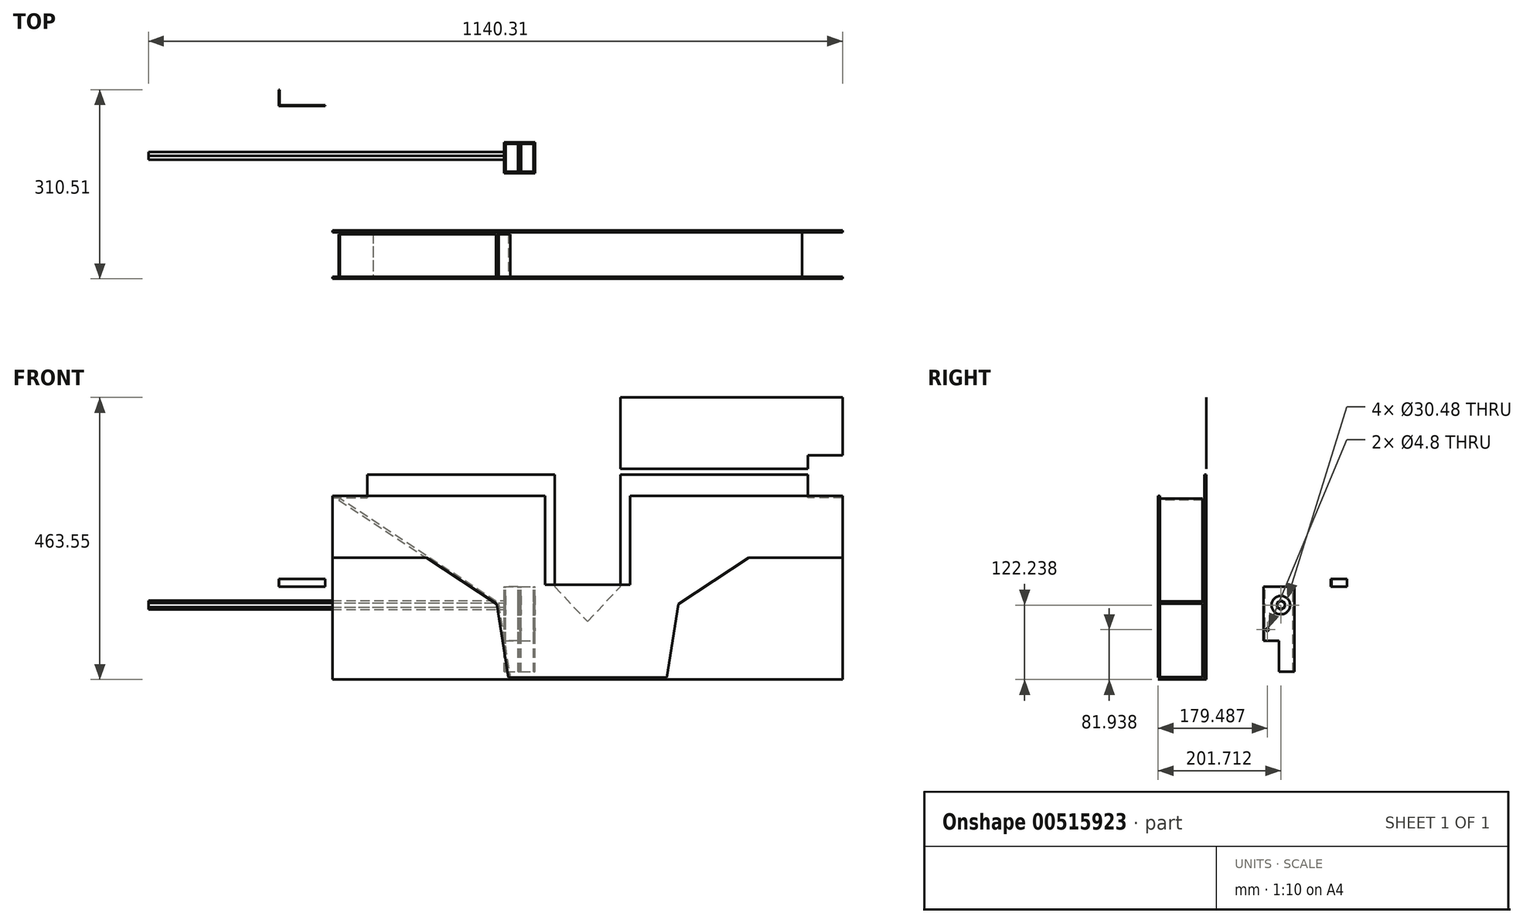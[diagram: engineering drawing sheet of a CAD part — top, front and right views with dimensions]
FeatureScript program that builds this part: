
annotation { "Feature Type Name" : "Feature", "Feature Type Description" : "" }
export const myFeature = defineFeature(function(context is Context, id is Id, definition is map)
    precondition{}
    {
        {
            var Q0;
            Q0=qCreatedBy(makeId("Front.planeOp"),FACE);
            var sketch = newSketch(context, id + "F0", { "sketchPlane" : qUnion([Q0])});
            skLineSegment(sketch, "E0", {"start": v(-365.13, 311.15) * mm, "end": v(-365.13, -152.4) * mm});
            skLineSegment(sketch, "E1", {"start": v(-365.13, -152.4) * mm, "end": v(473.07, -152.4) * mm});
            skLineSegment(sketch, "E2", {"start": v(473.07, 311.15) * mm, "end": v(473.07, -152.4) * mm});
            skLineSegment(sketch, "E3", {"start": v(0, 311.15) * mm, "end": v(0, 0) * mm});
            skLineSegment(sketch, "E4", {"start": v(0, 0) * mm, "end": v(107.95, 0) * mm});
            skLineSegment(sketch, "E5", {"start": v(107.95, 0) * mm, "end": v(107.95, 311.15) * mm});
            skLineSegment(sketch, "E6", {"start": v(0, 311.15) * mm, "end": v(-365.13, 311.15) * mm});
            skLineSegment(sketch, "E7", {"start": v(107.95, 311.15) * mm, "end": v(473.07, 311.15) * mm});
            skLineSegment(sketch, "E8", {"start": v(-365.13, 184.15) * mm, "end": v(0, 184.15) * mm});
            skLineSegment(sketch, "E9", {"start": v(107.95, 184.15) * mm, "end": v(473.07, 184.15) * mm});
            skLineSegment(sketch, "E10", {"start": v(107.95, 193.67) * mm, "end": v(473.07, 193.67) * mm});
            skLineSegment(sketch, "E11", {"start": v(0, 0) * mm, "end": v(53.97, -57.15) * mm});
            skLineSegment(sketch, "E12", {"start": v(53.97, -57.15) * mm, "end": v(107.95, 0) * mm});
            skSolve(sketch);
        }
        {
            var Q0;
            {var subQ1=sQuery(id+"F0.wireOp",EDGE,"E1");Q0=makeQuery(id+"F0.imprint","IMPRINT",FACE,{"disambiguationData":[TD([[makeQuery(id+"F0.imprint","IMPRINT",EDGE,{"derivedFrom":subQ1}),1.0]])]});}
            extrude(context, id + "F1", {"entities" : qUnion([Q0]), "depth" : 3.17 * mm});
        }
        {
            var Q0;
            Q0=makeQuery(id+"F1.opExtrude","SWEPT_FACE",FACE,{"disambiguationData":[OSD([sQuery(id+"F0.wireOp",EDGE,"E1")])]});
            var sketch = newSketch(context, id + "F2", { "sketchPlane" : qUnion([Q0])});
            skLineSegment(sketch, "E13.bottom", {"start": v(-298.45, 3.18) * mm, "end": v(406.4, 3.18) * mm});
            skLineSegment(sketch, "E13.top", {"start": v(-298.45, 79.37) * mm, "end": v(406.4, 79.37) * mm});
            skLineSegment(sketch, "E13.left", {"start": v(406.4, 3.18) * mm, "end": v(406.4, 79.37) * mm});
            skLineSegment(sketch, "E13.right", {"start": v(-298.45, 3.18) * mm, "end": v(-298.45, 79.37) * mm});
            skLineSegment(sketch, "E14", {"start": v(406.4, 3.18) * mm, "end": v(-365.13, 3.18) * mm, "construction": true});
            skLineSegment(sketch, "E15", {"start": v(-298.45, 3.17) * mm, "end": v(473.08, 0) * mm, "construction": true});
            skSolve(sketch);
        }
        {
            var Q0;
            Q0=makeQuery(id+"F2.imprint","IMPRINT",FACE,{"disambiguationData":[TD([[makeQuery(id+"F2.imprint","IMPRINT",EDGE,{"derivedFrom":sQuery(id+"F2.wireOp",EDGE,"E13.bottom")}),1.0]])]});
            extrude(context, id + "F3", {"entities" : qUnion([Q0]), "oppositeDirection" : true, "depth" : 1 / 203.2 * mm});
        }
        {
            var Q0;
            {var subQ0=sQuery(id+"F0.wireOp",EDGE,"E7");Q0=makeQuery(id+"F0.imprint","IMPRINT",FACE,{"disambiguationData":[TD([[makeQuery(id+"F0.imprint","IMPRINT",EDGE,{"derivedFrom":subQ0}),-1.0]])]});}
            extrude(context, id + "F4", {"entities" : qUnion([Q0]), "depth" : 1 / 203.2 * mm});
        }
        {
            var Q0;
            Q0=makeQuery(id+"F3.opExtrude","SWEPT_FACE",FACE,{"disambiguationData":[OSD([sQuery(id+"F2.wireOp",EDGE,"E13.top")])]});
            var sketch = newSketch(context, id + "F5", { "sketchPlane" : qUnion([Q0])});
            skLineSegment(sketch, "E16", {"start": v(-15.88, 149.22) * mm, "end": v(-365.13, 149.22) * mm});
            skLineSegment(sketch, "E17", {"start": v(-365.13, 149.23) * mm, "end": v(-95.25, -28.58) * mm});
            skLineSegment(sketch, "E18", {"start": v(-95.25, -28.57) * mm, "end": v(-76.2, -149.22) * mm});
            skLineSegment(sketch, "E19.MirrorCS", {"start": v(203.2, -28.58) * mm, "end": v(184.15, -149.22) * mm});
            skLineSegment(sketch, "E20.MirrorCS", {"start": v(473.07, 149.23) * mm, "end": v(203.2, -28.58) * mm});
            skLineSegment(sketch, "E21.MirrorCS", {"start": v(123.82, 149.23) * mm, "end": v(473.07, 149.23) * mm});
            skLineSegment(sketch, "E22", {"start": v(-76.2, -149.23) * mm, "end": v(184.15, -149.22) * mm});
            skPoint(sketch, "E23", {"position": v(53.98, -152.4) * mm});
            skLineSegment(sketch, "E24", {"start": v(-15.88, 149.22) * mm, "end": v(-15.88, 3.17) * mm});
            skLineSegment(sketch, "E25", {"start": v(123.82, 149.23) * mm, "end": v(123.82, 3.18) * mm});
            skLineSegment(sketch, "E26", {"start": v(-365.13, 149.22) * mm, "end": v(-365.13, 47.62) * mm});
            skLineSegment(sketch, "E27", {"start": v(-365.13, 47.62) * mm, "end": v(-210.91, 47.62) * mm});
            skLineSegment(sketch, "E28", {"start": v(473.07, 149.23) * mm, "end": v(473.07, 47.62) * mm});
            skLineSegment(sketch, "E29", {"start": v(473.07, 47.62) * mm, "end": v(318.86, 47.62) * mm});
            skLineSegment(sketch, "E30", {"start": v(-95.25, -28.58) * mm, "end": v(203.2, -28.58) * mm, "construction": true});
            skLineSegment(sketch, "E31", {"start": v(123.82, 3.18) * mm, "end": v(-15.88, 3.17) * mm});
            skSolve(sketch);
        }
        {
            var Q0;
            Q0=makeQuery(id+"F5.imprint","IMPRINT",FACE,{"disambiguationData":[TD([[makeQuery(id+"F5.imprint","IMPRINT",EDGE,{"derivedFrom":sQuery(id+"F5.wireOp",EDGE,"E16")}),1.0]])]});
            var Q1;
            {var subQ0=sQuery(id+"F5.wireOp",EDGE,"E26");Q1=makeQuery(id+"F5.imprint","IMPRINT",FACE,{"disambiguationData":[TD([[makeQuery(id+"F5.imprint","IMPRINT",EDGE,{"derivedFrom":subQ0}),1.0]])]});}
            var Q2;
            {var subQ0=sQuery(id+"F5.wireOp",EDGE,"E28");Q2=makeQuery(id+"F5.imprint","IMPRINT",FACE,{"disambiguationData":[TD([[makeQuery(id+"F5.imprint","IMPRINT",EDGE,{"derivedFrom":subQ0}),-1.0]])]});}
            extrude(context, id + "F6", {"entities" : qUnion([Q0, Q1, Q2]), "oppositeDirection" : true, "depth" : 3.17 * mm});
        }
        {
            var Q0;
            Q0=makeQuery(id+"F6.opExtrude","CAP_FACE",FACE,{"disambiguationData":[OSD([sQuery(id+"F5.wireOp",EDGE,"E16"),sQuery(id+"F5.wireOp",EDGE,"E17"),sQuery(id+"F5.wireOp",EDGE,"E18"),sQuery(id+"F5.wireOp",EDGE,"E19.MirrorCS"),sQuery(id+"F5.wireOp",EDGE,"E20.MirrorCS"),sQuery(id+"F5.wireOp",EDGE,"E21.MirrorCS"),sQuery(id+"F5.wireOp",EDGE,"E22"),sQuery(id+"F5.wireOp",EDGE,"E24"),sQuery(id+"F5.wireOp",EDGE,"E25"),sQuery(id+"F5.wireOp",EDGE,"bJVduE53-CYSX-zZap-hoKB-BpQSyu4JU1O0"),sQuery(id+"F5.wireOp",EDGE,"kxEBCK4Z-cyDY-w3D9-cJRx-P5z5Afn2VGam")])],"isStart":false});
            var sketch = newSketch(context, id + "F7", { "sketchPlane" : qUnion([Q0])});
            skLineSegment(sketch, "E32.bottom", {"start": v(95.25, -28.58) * mm, "end": v(92.11, -28.08) * mm});
            skLineSegment(sketch, "E32.top", {"start": v(76.2, -149.23) * mm, "end": v(73.06, -148.73) * mm});
            skLineSegment(sketch, "E32.left", {"start": v(95.25, -28.57) * mm, "end": v(76.2, -149.23) * mm});
            skLineSegment(sketch, "E32.right", {"start": v(92.11, -28.08) * mm, "end": v(73.06, -148.73) * mm});
            skSolve(sketch);
        }
        {
            var Q0;
            Q0 = qSketchRegion(id + "F7", true);
            extrude(context, id + "F8", {"entities" : qUnion([Q0]), "depth" : 69.85 * mm});
        }
        {
            var Q0;
            Q0=makeQuery(id+"F6.opExtrude","CAP_FACE",FACE,{"disambiguationData":[OSD([sQuery(id+"F5.wireOp",EDGE,"E16"),sQuery(id+"F5.wireOp",EDGE,"E17"),sQuery(id+"F5.wireOp",EDGE,"E18"),sQuery(id+"F5.wireOp",EDGE,"E19.MirrorCS"),sQuery(id+"F5.wireOp",EDGE,"E20.MirrorCS"),sQuery(id+"F5.wireOp",EDGE,"E21.MirrorCS"),sQuery(id+"F5.wireOp",EDGE,"E22"),sQuery(id+"F5.wireOp",EDGE,"E24"),sQuery(id+"F5.wireOp",EDGE,"E25"),sQuery(id+"F5.wireOp",EDGE,"bJVduE53-CYSX-zZap-hoKB-BpQSyu4JU1O0"),sQuery(id+"F5.wireOp",EDGE,"kxEBCK4Z-cyDY-w3D9-cJRx-P5z5Afn2VGam"),sQuery(id+"F5.wireOp",EDGE,"E26"),sQuery(id+"F5.wireOp",EDGE,"E27"),sQuery(id+"F5.wireOp",EDGE,"E28"),sQuery(id+"F5.wireOp",EDGE,"E29")])],"isStart":false});
            var sketch = newSketch(context, id + "F9", { "sketchPlane" : qUnion([Q0])});
            skLineSegment(sketch, "E33.0", {"start": v(365.13, 149.23) * mm, "end": v(95.25, -28.58) * mm});
            skLineSegment(sketch, "E34.bottom", {"start": v(352.77, 144.89) * mm, "end": v(354.52, 142.24) * mm});
            skLineSegment(sketch, "E34.top", {"start": v(96.15, -24.18) * mm, "end": v(97.9, -26.83) * mm});
            skLineSegment(sketch, "E34.left", {"start": v(97.9, -26.83) * mm, "end": v(354.52, 142.24) * mm});
            skLineSegment(sketch, "E34.right", {"start": v(96.15, -24.18) * mm, "end": v(352.77, 144.89) * mm});
            skSolve(sketch);
        }
        {
            var Q0;
            {var subQ2=sQuery(id+"F9.wireOp",EDGE,"E34.bottom");Q0=makeQuery(id+"F9.imprint","IMPRINT",FACE,{"disambiguationData":[TD([[makeQuery(id+"F9.imprint","IMPRINT",EDGE,{"derivedFrom":subQ2}),-1.0]])]});}
            extrude(context, id + "F10", {"entities" : qUnion([Q0]), "depth" : 69.85 * mm});
        }
        {
            var Q0;
            Q0=qCreatedBy(makeId("Top.planeOp"),FACE);
            var sketch = newSketch(context, id + "F11", { "sketchPlane" : qUnion([Q0])});
            skLineSegment(sketch, "E35.bottom", {"start": v(-57.63, 144.56) * mm, "end": v(-32.23, 144.56) * mm});
            skLineSegment(sketch, "E35.top", {"start": v(-57.63, 93.76) * mm, "end": v(-32.23, 93.76) * mm});
            skLineSegment(sketch, "E35.left", {"start": v(-57.63, 144.56) * mm, "end": v(-57.63, 93.76) * mm});
            skLineSegment(sketch, "E35.right", {"start": v(-32.23, 144.56) * mm, "end": v(-32.23, 93.76) * mm});
            skLineSegment(sketch, "E36.bottom", {"start": v(-55.1, 142.02) * mm, "end": v(-34.77, 142.02) * mm});
            skLineSegment(sketch, "E36.top", {"start": v(-55.1, 96.3) * mm, "end": v(-34.77, 96.3) * mm});
            skLineSegment(sketch, "E36.left", {"start": v(-55.1, 142.02) * mm, "end": v(-55.1, 96.3) * mm});
            skLineSegment(sketch, "E36.right", {"start": v(-34.77, 142.02) * mm, "end": v(-34.77, 96.3) * mm});
            skSolve(sketch);
        }
        {
            var Q0;
            Q0=makeQuery(id+"F11.imprint","IMPRINT",FACE,{"disambiguationData":[TD([[makeQuery(id+"F11.imprint","IMPRINT",EDGE,{"derivedFrom":sQuery(id+"F11.wireOp",EDGE,"E35.bottom")}),-1.0]])]});
            extrude(context, id + "F12", {"entities" : qUnion([Q0]), "oppositeDirection" : true, "depth" : 88.9 * mm});
        }
        {
            var Q0;
            Q0=makeQuery(id+"F12.opExtrude","SWEPT_FACE",FACE,{"disambiguationData":[OSD([sQuery(id+"F11.wireOp",EDGE,"E35.left")])]});
            var sketch = newSketch(context, id + "F13", { "sketchPlane" : qUnion([Q0])});
            skCircle(sketch, "E37", {"center": v(-122.33, -30.16) * mm, "radius": 15.24 * mm});
            skCircle(sketch, "E38", {"center": v(-100.1, -70.46) * mm, "radius": 2.4 * mm});
            skLineSegment(sketch, "E39.0", {"start": v(-93.76, -88.9) * mm, "end": v(-93.76, 0) * mm});
            skSolve(sketch);
        }
        {
            var Q0;
            Q0=makeQuery(id+"F13.imprint","IMPRINT",FACE,{"disambiguationData":[TD([[makeQuery(id+"F13.imprint","IMPRINT",EDGE,{"derivedFrom":sQuery(id+"F13.wireOp",EDGE,"E37")}),1.0]])]});
            var Q1;
            Q1=makeQuery(id+"F13.imprint","IMPRINT",FACE,{"disambiguationData":[TD([[makeQuery(id+"F13.imprint","IMPRINT",EDGE,{"derivedFrom":sQuery(id+"F13.wireOp",EDGE,"E38")}),1.0]])]});
            var Q2;
            Q2=makeQuery(id+"F12.opExtrude","SWEPT_FACE",FACE,{"disambiguationData":[OSD([sQuery(id+"F11.wireOp",EDGE,"E35.right")])]});
            extrude(context, id + "F14", {"entities" : qUnion([Q0, Q1]), "operationType" : NewBodyOperationType.REMOVE, "endBound" : BoundingType.UP_TO_SURFACE, "oppositeDirection" : true, "endBoundEntityFace" : qUnion([Q2]), "depth" : 25.4 * mm});
        }
        {
            var Q0;
            Q0=makeQuery(id+"F12.opExtrude","SWEPT_FACE",FACE,{"disambiguationData":[OSD([sQuery(id+"F11.wireOp",EDGE,"E35.left")])]});
            var sketch = newSketch(context, id + "F15", { "sketchPlane" : qUnion([Q0])});
            skCircle(sketch, "E40.cCircle", {"center": v(-122.33, -30.16) * mm, "radius": 6.35 * mm, "construction": true});
            skLineSegment(sketch, "E40.0", {"start": v(-115.98, -33.83) * mm, "end": v(-122.33, -37.5) * mm});
            skLineSegment(sketch, "E40.1", {"start": v(-122.33, -37.5) * mm, "end": v(-128.68, -33.83) * mm});
            skLineSegment(sketch, "E40.2", {"start": v(-128.68, -33.83) * mm, "end": v(-128.68, -26.5) * mm});
            skLineSegment(sketch, "E40.3", {"start": v(-128.68, -26.5) * mm, "end": v(-122.33, -22.83) * mm});
            skLineSegment(sketch, "E40.4", {"start": v(-122.33, -22.83) * mm, "end": v(-115.98, -26.5) * mm});
            skLineSegment(sketch, "E40.5", {"start": v(-115.98, -26.5) * mm, "end": v(-115.98, -33.83) * mm});
            skPoint(sketch, "E40.0.midPoint", {"position": v(-119.16, -35.66) * mm});
            skSolve(sketch);
        }
        {
            var Q0;
            Q0=makeQuery(id+"F15.imprint","IMPRINT",FACE,{"disambiguationData":[TD([[makeQuery(id+"F15.imprint","IMPRINT",EDGE,{"derivedFrom":sQuery(id+"F15.wireOp",EDGE,"E40.0")}),-1.0]])]});
            extrude(context, id + "F16", {"entities" : qUnion([Q0]), "depth" : 609.6 * mm});
        }
        {
            var Q0;
            {var subQ1=sQuery(id+"F0.wireOp",EDGE,"E1");Q0=makeQuery(id+"F0.imprint","IMPRINT",FACE,{"disambiguationData":[TD([[makeQuery(id+"F0.imprint","IMPRINT",EDGE,{"derivedFrom":subQ1}),1.0]])]});}
            var sketch = newSketch(context, id + "F17", { "sketchPlane" : qUnion([Q0])});
            skLineSegment(sketch, "E41.bottom", {"start": v(473.07, 146.05) * mm, "end": v(415.92, 146.05) * mm});
            skLineSegment(sketch, "E41.top", {"start": v(473.07, 215.9) * mm, "end": v(415.92, 215.9) * mm});
            skLineSegment(sketch, "E41.left", {"start": v(473.07, 146.05) * mm, "end": v(473.07, 215.9) * mm});
            skLineSegment(sketch, "E41.right", {"start": v(415.92, 146.05) * mm, "end": v(415.92, 215.9) * mm});
            skLineSegment(sketch, "E42.0", {"start": v(107.95, 184.15) * mm, "end": v(473.07, 184.15) * mm});
            skLineSegment(sketch, "E43.bottom", {"start": v(-365.13, 184.15) * mm, "end": v(-307.98, 184.15) * mm});
            skLineSegment(sketch, "E43.top", {"start": v(-365.13, 146.05) * mm, "end": v(-307.98, 146.05) * mm});
            skLineSegment(sketch, "E43.left", {"start": v(-365.13, 184.15) * mm, "end": v(-365.13, 146.05) * mm});
            skLineSegment(sketch, "E43.right", {"start": v(-307.98, 184.15) * mm, "end": v(-307.98, 146.05) * mm});
            skSolve(sketch);
        }
        {
            var Q0;
            Q0=qSketchRegion(id+"F17",true);
            var Q1;
            Q1=qConstructionFilter(qBodyType(qCreatedBy(id+"F17",EDGE),BodyType.WIRE),ConstructionObject.NO);
            var Q2;
            Q2=makeQuery(id+"F1.opExtrude","CAP_FACE",FACE,{"disambiguationData":[OSD([sQuery(id+"F0.wireOp",EDGE,"E0"),sQuery(id+"F0.wireOp",EDGE,"E1"),sQuery(id+"F0.wireOp",EDGE,"E2"),sQuery(id+"F0.wireOp",EDGE,"E3"),sQuery(id+"F0.wireOp",EDGE,"E4"),sQuery(id+"F0.wireOp",EDGE,"E5"),sQuery(id+"F0.wireOp",EDGE,"E8"),sQuery(id+"F0.wireOp",EDGE,"E9")])],"isStart":false});
            extrude(context, id + "F18", {"entities" : qUnion([Q0]), "operationType" : NewBodyOperationType.REMOVE, "surfaceEntities" : qUnion([Q1]), "endBound" : BoundingType.UP_TO_SURFACE, "endBoundEntityFace" : qUnion([Q2]), "depth" : 25.4 * mm});
        }
        {
            var Q0;
            Q0=qCreatedBy(makeId("Top.planeOp"),FACE);
            var sketch = newSketch(context, id + "F19", { "sketchPlane" : qUnion([Q0])});
            skLineSegment(sketch, "E44", {"start": v(-453.06, 231.13) * mm, "end": v(-453.06, 204.46) * mm});
            skLineSegment(sketch, "E45", {"start": v(-453.06, 204.46) * mm, "end": v(-376.86, 204.46) * mm});
            skLineSegment(sketch, "E46", {"start": v(-376.86, 204.46) * mm, "end": v(-376.86, 205.73) * mm});
            skLineSegment(sketch, "E47", {"start": v(-376.86, 205.73) * mm, "end": v(-451.79, 205.73) * mm});
            skLineSegment(sketch, "E48", {"start": v(-451.79, 205.73) * mm, "end": v(-451.79, 231.13) * mm});
            skLineSegment(sketch, "E49", {"start": v(-451.79, 231.13) * mm, "end": v(-453.06, 231.13) * mm});
            skSolve(sketch);
        }
        {
            var Q0;
            Q0=makeQuery(id+"F19.imprint","IMPRINT",FACE,{"disambiguationData":[TD([[makeQuery(id+"F19.imprint","IMPRINT",EDGE,{"derivedFrom":sQuery(id+"F19.wireOp",EDGE,"E44")}),1.0]])]});
            extrude(context, id + "F20", {"entities" : qUnion([Q0]), "depth" : 12.7 * mm});
        }
        {
            var Q0;
            Q0=makeQuery(id+"F12.opExtrude","CAP_FACE",FACE,{"disambiguationData":[OSD([sQuery(id+"F11.wireOp",EDGE,"E35.bottom"),sQuery(id+"F11.wireOp",EDGE,"E35.top"),sQuery(id+"F11.wireOp",EDGE,"E35.left"),sQuery(id+"F11.wireOp",EDGE,"E35.right"),sQuery(id+"F11.wireOp",EDGE,"E36.bottom"),sQuery(id+"F11.wireOp",EDGE,"E36.top"),sQuery(id+"F11.wireOp",EDGE,"E36.left"),sQuery(id+"F11.wireOp",EDGE,"E36.right")])],"isStart":false});
            var sketch = newSketch(context, id + "F21", { "sketchPlane" : qUnion([Q0])});
            skLineSegment(sketch, "E50.0", {"start": v(-55.1, -142.02) * mm, "end": v(-34.77, -142.02) * mm});
            skLineSegment(sketch, "E50.1", {"start": v(-34.77, -142.02) * mm, "end": v(-34.77, -96.3) * mm});
            skLineSegment(sketch, "E50.2", {"start": v(-55.1, -142.02) * mm, "end": v(-55.1, -96.3) * mm});
            skLineSegment(sketch, "E50.3", {"start": v(-57.63, -144.56) * mm, "end": v(-57.63, -93.76) * mm});
            skLineSegment(sketch, "E50.4", {"start": v(-57.63, -144.56) * mm, "end": v(-32.23, -144.56) * mm});
            skLineSegment(sketch, "E50.5", {"start": v(-32.23, -144.56) * mm, "end": v(-32.23, -93.76) * mm});
            skLineSegment(sketch, "E51", {"start": v(-32.23, -119.16) * mm, "end": v(-57.63, -119.16) * mm});
            skSolve(sketch);
        }
        {
            var Q0;
            {var subQ1=sQuery(id+"F21.wireOp",EDGE,"E50.0");Q0=makeQuery(id+"F21.imprint","IMPRINT",FACE,{"disambiguationData":[TD([[makeQuery(id+"F21.imprint","IMPRINT",EDGE,{"derivedFrom":subQ1}),-1.0]])]});}
            extrude(context, id + "F22", {"entities" : qUnion([Q0]), "operationType" : NewBodyOperationType.ADD, "depth" : 50.8 * mm});
        }
        {
            var Q0;
            Q0=makeQuery(id+"F22.boolean.opBoolean","MERGE",FACE,{"derivedFrom":[makeQuery(id+"F12.opExtrude","SWEPT_FACE",FACE,{"disambiguationData":[OSD([sQuery(id+"F11.wireOp",EDGE,"E35.left")])]}),makeQuery(id+"F22.opExtrude","SWEPT_FACE",FACE,{"disambiguationData":[OSD([sQuery(id+"F21.wireOp",EDGE,"E50.3")])]})]});
            var sketch = newSketch(context, id + "F23", { "sketchPlane" : qUnion([Q0])});
            skCircle(sketch, "E52.0", {"center": v(-122.33, -30.16) * mm, "radius": 15.24 * mm});
            skLineSegment(sketch, "E52.1", {"start": v(-119.16, -88.9) * mm, "end": v(-93.76, -88.9) * mm});
            skLineSegment(sketch, "E52.2", {"start": v(-93.76, -88.9) * mm, "end": v(-93.76, 0) * mm});
            skLineSegment(sketch, "E52.3", {"start": v(-119.16, -139.7) * mm, "end": v(-119.16, -88.9) * mm});
            skLineSegment(sketch, "E52.4", {"start": v(-144.56, -139.7) * mm, "end": v(-119.16, -139.7) * mm});
            skLineSegment(sketch, "E52.5", {"start": v(-144.56, -139.7) * mm, "end": v(-144.56, 0) * mm});
            skLineSegment(sketch, "E52.6", {"start": v(-144.56, 0) * mm, "end": v(-93.76, 0) * mm});
            skSolve(sketch);
        }
        {
            var Q0;
            Q0=qSketchRegion(id+"F23",true);
            extrude(context, id + "F24", {"entities" : qUnion([Q0]), "depth" : 25.4 * mm});
        }
        {
            var Q0;
            Q0=makeQuery(id+"F24.opExtrude","SWEPT_FACE",FACE,{"disambiguationData":[OSD([sQuery(id+"F23.wireOp",EDGE,"E52.6")])]});
            var sketch = newSketch(context, id + "F25", { "sketchPlane" : qUnion([Q0])});
            skLineSegment(sketch, "E53.bottom", {"start": v(-60.17, 142.02) * mm, "end": v(-80.5, 142.02) * mm});
            skLineSegment(sketch, "E53.top", {"start": v(-60.17, 96.3) * mm, "end": v(-80.5, 96.3) * mm});
            skLineSegment(sketch, "E53.left", {"start": v(-60.17, 142.02) * mm, "end": v(-60.17, 96.3) * mm});
            skLineSegment(sketch, "E53.right", {"start": v(-80.5, 142.02) * mm, "end": v(-80.5, 96.3) * mm});
            skSolve(sketch);
        }
        {
            var Q0;
            Q0=makeQuery(id+"F25.imprint","IMPRINT",FACE,{"disambiguationData":[TD([[makeQuery(id+"F25.imprint","IMPRINT",EDGE,{"derivedFrom":sQuery(id+"F25.wireOp",EDGE,"E53.bottom")}),1.0]])]});
            var Q1;
            Q1=makeQuery(id+"F24.opExtrude","SWEPT_FACE",FACE,{"disambiguationData":[OSD([sQuery(id+"F23.wireOp",EDGE,"E52.4")])]});
            extrude(context, id + "F26", {"entities" : qUnion([Q0]), "operationType" : NewBodyOperationType.REMOVE, "endBound" : BoundingType.UP_TO_SURFACE, "oppositeDirection" : true, "endBoundEntityFace" : qUnion([Q1]), "depth" : 25.4 * mm});
        }
    });
